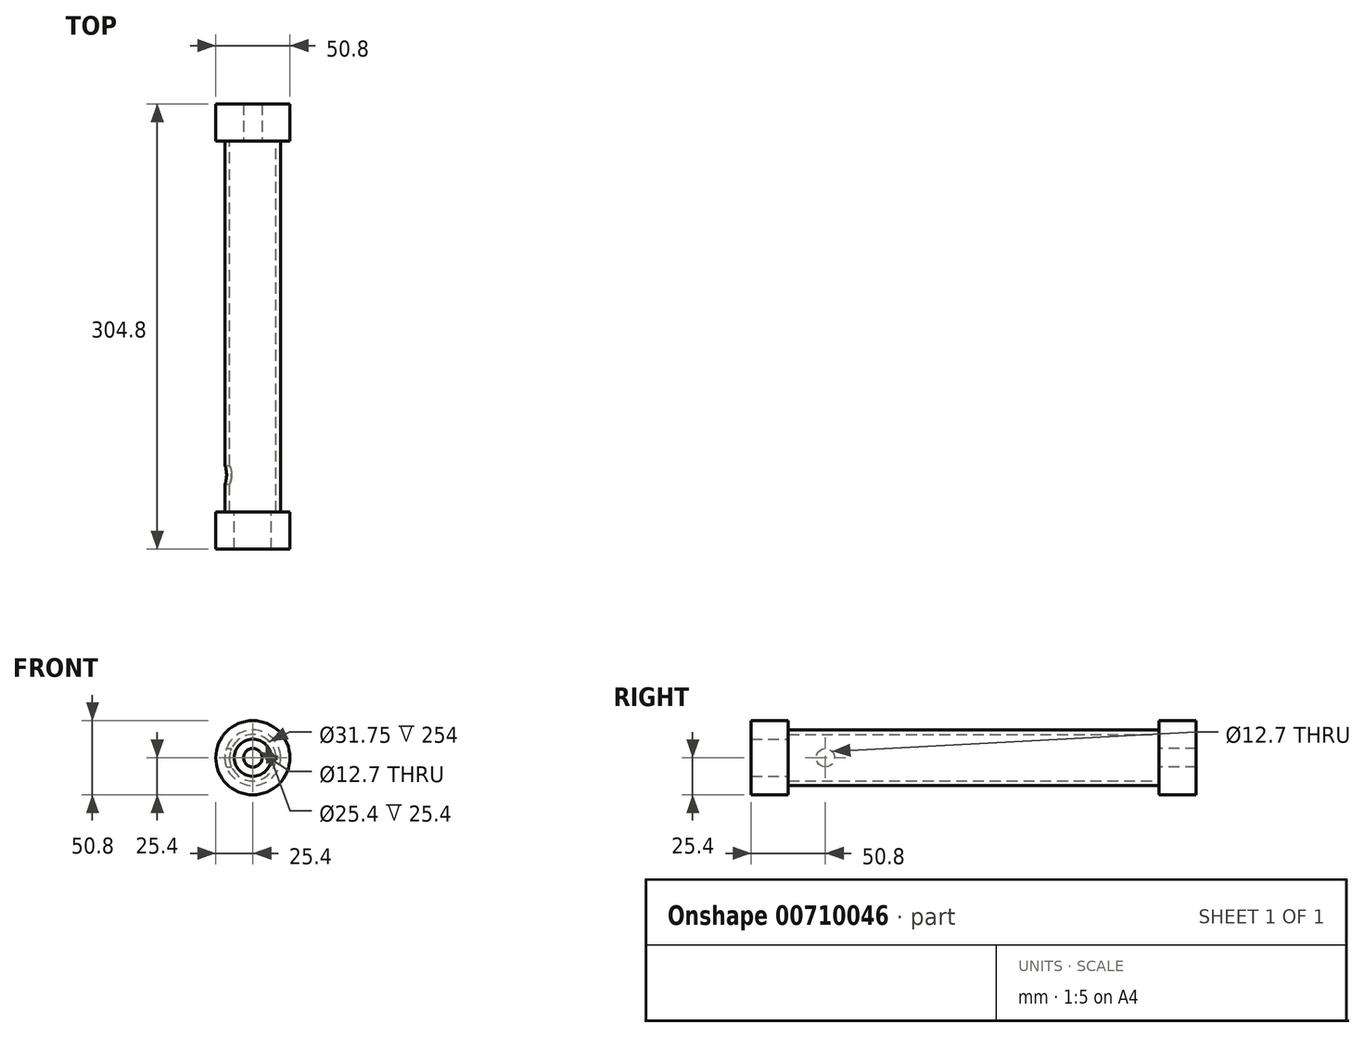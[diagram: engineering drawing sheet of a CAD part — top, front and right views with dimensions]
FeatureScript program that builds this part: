
annotation { "Feature Type Name" : "Feature", "Feature Type Description" : "" }
export const myFeature = defineFeature(function(context is Context, id is Id, definition is map)
    precondition{}
    {
        {
            var Q0;
            Q0=qCreatedBy(makeId("Front.planeOp"),FACE);
            var sketch = newSketch(context, id + "F0", { "sketchPlane" : qUnion([Q0])});
            skCircle(sketch, "E0", {"center": v(0, 0) * mm, "radius": 15.88 * mm});
            skCircle(sketch, "E1", {"center": v(0, 0) * mm, "radius": 19.05 * mm});
            skSolve(sketch);
        }
        {
            var Q0;
            Q0=makeQuery(id+"F0.imprint","IMPRINT",FACE,{"disambiguationData":[TD([[makeQuery(id+"F0.imprint","IMPRINT",EDGE,{"derivedFrom":sQuery(id+"F0.wireOp",EDGE,"E0")}),-1.0]])]});
            extrude(context, id + "F1", {"entities" : qUnion([Q0]), "depth" : 254 * mm, "offsetDistance" : 25.4 * mm});
        }
        {
            var Q0;
            Q0=makeQuery(id+"F1.opExtrude","CAP_FACE",FACE,{"disambiguationData":[OSD([sQuery(id+"F0.wireOp",EDGE,"E0"),sQuery(id+"F0.wireOp",EDGE,"E1")])],"isStart":true});
            var sketch = newSketch(context, id + "F2", { "sketchPlane" : qUnion([Q0])});
            skCircle(sketch, "E2", {"center": v(0, 0) * mm, "radius": 25.4 * mm});
            skCircle(sketch, "E3", {"center": v(0, 0) * mm, "radius": 6.35 * mm});
            skSolve(sketch);
        }
        {
            var Q0;
            Q0 = qSketchRegion(id + "F2", true);
            extrude(context, id + "F3", {"entities" : qUnion([Q0]), "operationType" : NewBodyOperationType.ADD, "depth" : 25.4 * mm, "offsetDistance" : 25.4 * mm});
        }
        {
            var Q0;
            Q0=makeQuery(id+"F1.opExtrude","CAP_FACE",FACE,{"disambiguationData":[OSD([sQuery(id+"F0.wireOp",EDGE,"E0"),sQuery(id+"F0.wireOp",EDGE,"E1")])],"isStart":false});
            var sketch = newSketch(context, id + "F4", { "sketchPlane" : qUnion([Q0])});
            skCircle(sketch, "E4", {"center": v(0, 0) * mm, "radius": 25.4 * mm});
            skCircle(sketch, "E5", {"center": v(0, 0) * mm, "radius": 12.7 * mm});
            skSolve(sketch);
        }
        {
            var Q0;
            Q0 = qSketchRegion(id + "F4", true);
            extrude(context, id + "F5", {"entities" : qUnion([Q0]), "operationType" : NewBodyOperationType.ADD, "depth" : 25.4 * mm, "offsetDistance" : 25.4 * mm});
        }
        {
            var Q0;
            Q0=qCreatedBy(makeId("Right.planeOp"),FACE);
            var sketch = newSketch(context, id + "F6", { "sketchPlane" : qUnion([Q0])});
            skCircle(sketch, "E6", {"center": v(-228.6, 0) * mm, "radius": 6.35 * mm});
            skSolve(sketch);
        }
        {
            var Q0;
            Q0=sQuery(id+"F6.wireOp",VERTEX,"E6.center");
            var Q1;
            Q1=makeQuery(id+"F1.opExtrude","SWEPT_BODY",BODY,{"disambiguationData":[OSD([sQuery(id+"F0.wireOp",EDGE,"E0"),sQuery(id+"F0.wireOp",EDGE,"E1")])]});
            hole(context, id + "F7", {"style" : HoleStyle.SIMPLE, "endStyle" : HoleEndStyle.THROUGH, "holeDiameter" : 12.7 * mm, "majorDiameter" : 6.35 * mm, "isTappedThrough" : true, "tappedDepth" : 12.7 * mm, "tapClearance" : 3, "locations" : qUnion([Q0]), "scope" : qUnion([Q1])});
        }
    });
